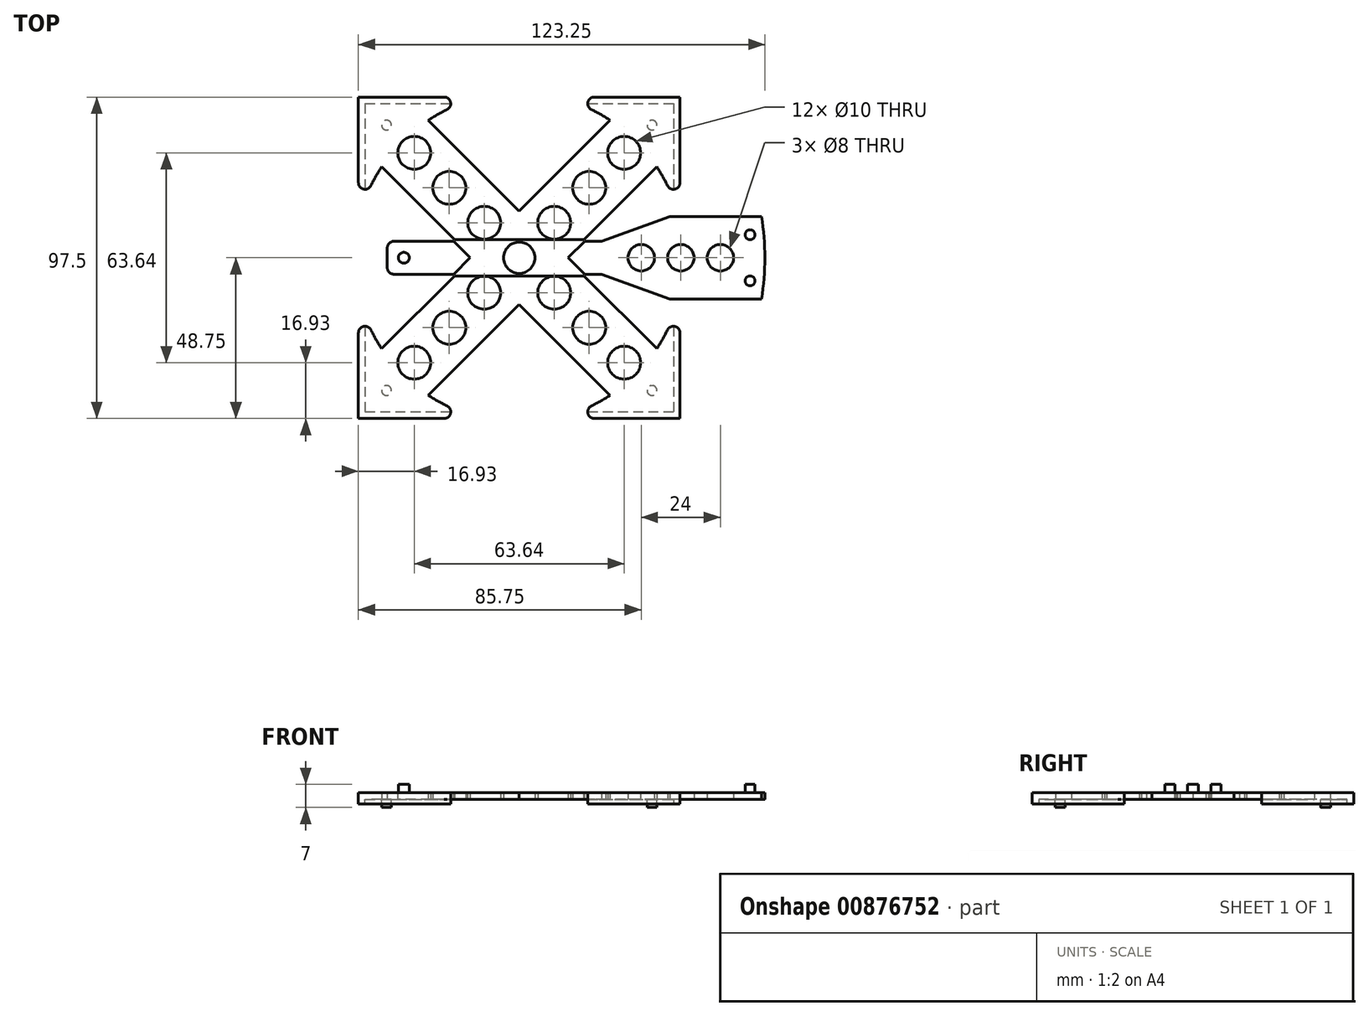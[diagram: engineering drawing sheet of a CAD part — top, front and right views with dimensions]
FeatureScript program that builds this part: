
annotation { "Feature Type Name" : "Feature", "Feature Type Description" : "" }
export const myFeature = defineFeature(function(context is Context, id is Id, definition is map)
    precondition{}
    {
        {
            var Q0;
            Q0=qCreatedBy(makeId("Top.planeOp"),FACE);
            var sketch = newSketch(context, id + "F0", { "sketchPlane" : qUnion([Q0])});
            skLineSegment(sketch, "E0.bottom", {"start": v(-48.75, 48.75) * mm, "end": v(-11.11, 48.75) * mm});
            skLineSegment(sketch, "E0.top", {"start": v(-48.75, -48.75) * mm, "end": v(-11.11, -48.75) * mm});
            skLineSegment(sketch, "E0.left", {"start": v(-48.75, 48.75) * mm, "end": v(-48.75, 11.11) * mm});
            skLineSegment(sketch, "E0.right", {"start": v(48.75, 48.75) * mm, "end": v(48.75, 11.11) * mm});
            skPoint(sketch, "E0.middle", {"position": v(0, 0) * mm});
            skLineSegment(sketch, "E1.trimOffspring", {"start": v(-48.75, -11.11) * mm, "end": v(-48.75, -48.75) * mm});
            skLineSegment(sketch, "E2.trimOffspring", {"start": v(48.75, -11.11) * mm, "end": v(48.75, -48.75) * mm});
            skArc(sketch, "E3", {"start": v(-11.11, 48.75) * mm, "mid": v(-19.66, 45.97) * mm, "end": v(-27.57, 41.71) * mm});
            skLineSegment(sketch, "E4", {"start": v(-41.71, 27.57) * mm, "end": v(-14.14, 0) * mm});
            skLineSegment(sketch, "E5", {"start": v(41.71, -27.57) * mm, "end": v(14.14, 0) * mm});
            skLineSegment(sketch, "E6", {"start": v(27.57, 41.71) * mm, "end": v(0, 14.14) * mm});
            skLineSegment(sketch, "E7", {"start": v(-27.57, -41.71) * mm, "end": v(0, -14.14) * mm});
            skLineSegment(sketch, "E8.trimOffspring", {"start": v(11.11, 48.75) * mm, "end": v(48.75, 48.75) * mm});
            skArc(sketch, "E9.trimOffspring", {"start": v(11.11, -48.75) * mm, "mid": v(19.66, -45.97) * mm, "end": v(27.57, -41.71) * mm});
            skLineSegment(sketch, "E10.trimOffspring", {"start": v(11.11, -48.75) * mm, "end": v(48.75, -48.75) * mm});
            skArc(sketch, "E11.trimOffspring", {"start": v(-48.75, -11.11) * mm, "mid": v(-45.97, -19.66) * mm, "end": v(-41.71, -27.57) * mm});
            skLineSegment(sketch, "E12", {"start": v(0, -14.14) * mm, "end": v(0, 14.14) * mm, "construction": true});
            skLineSegment(sketch, "E13", {"start": v(-14.14, 0) * mm, "end": v(14.14, 0) * mm, "construction": true});
            skArc(sketch, "E14.trimOffspring", {"start": v(27.57, 41.71) * mm, "mid": v(19.66, 45.97) * mm, "end": v(11.11, 48.75) * mm});
            skArc(sketch, "E15.trimOffspring", {"start": v(-41.71, 27.57) * mm, "mid": v(-45.97, 19.66) * mm, "end": v(-48.75, 11.11) * mm});
            skArc(sketch, "E16.trimOffspring", {"start": v(-27.57, -41.71) * mm, "mid": v(-19.66, -45.97) * mm, "end": v(-11.11, -48.75) * mm});
            skLineSegment(sketch, "E17.trimOffspring", {"start": v(0, 14.14) * mm, "end": v(-27.57, 41.71) * mm});
            skLineSegment(sketch, "E18.trimOffspring", {"start": v(-14.14, 0) * mm, "end": v(-41.71, -27.57) * mm});
            skLineSegment(sketch, "E19.trimOffspring", {"start": v(0, -14.14) * mm, "end": v(27.57, -41.71) * mm});
            skLineSegment(sketch, "E20.trimOffspring", {"start": v(14.14, 0) * mm, "end": v(41.71, 27.57) * mm});
            skArc(sketch, "E21", {"start": v(48.75, 11.11) * mm, "mid": v(45.97, 19.66) * mm, "end": v(41.71, 27.57) * mm});
            skArc(sketch, "E22", {"start": v(41.71, -27.57) * mm, "mid": v(45.97, -19.66) * mm, "end": v(48.75, -11.11) * mm});
            skCircle(sketch, "E23", {"center": v(0, 0) * mm, "radius": 5 * mm});
            skCircle(sketch, "E24", {"center": v(-31.82, 31.82) * mm, "radius": 5 * mm});
            skCircle(sketch, "E25", {"center": v(-21.21, 21.21) * mm, "radius": 5 * mm});
            skCircle(sketch, "E26", {"center": v(-10.6, 10.6) * mm, "radius": 5 * mm});
            skCircle(sketch, "E27", {"center": v(10.6, -10.6) * mm, "radius": 5 * mm});
            skCircle(sketch, "E28", {"center": v(21.21, -21.21) * mm, "radius": 5 * mm});
            skCircle(sketch, "E29", {"center": v(31.82, -31.82) * mm, "radius": 5 * mm});
            skCircle(sketch, "E30", {"center": v(-10.6, -10.6) * mm, "radius": 5 * mm});
            skCircle(sketch, "E31", {"center": v(-21.21, -21.21) * mm, "radius": 5 * mm});
            skCircle(sketch, "E32", {"center": v(-31.82, -31.82) * mm, "radius": 5 * mm});
            skCircle(sketch, "E33", {"center": v(31.82, 31.82) * mm, "radius": 5 * mm});
            skCircle(sketch, "E34", {"center": v(21.21, 21.21) * mm, "radius": 5 * mm});
            skCircle(sketch, "E35", {"center": v(10.6, 10.6) * mm, "radius": 5 * mm});
            skLineSegment(sketch, "E36", {"start": v(0, 0) * mm, "end": v(-10.6, 10.6) * mm, "construction": true});
            skLineSegment(sketch, "E37", {"start": v(-10.6, 10.6) * mm, "end": v(-21.21, 21.21) * mm, "construction": true});
            skLineSegment(sketch, "E38", {"start": v(-21.21, 21.21) * mm, "end": v(-31.82, 31.82) * mm, "construction": true});
            skLineSegment(sketch, "E39", {"start": v(0, 0) * mm, "end": v(10.6, -10.6) * mm, "construction": true});
            skLineSegment(sketch, "E40", {"start": v(10.6, -10.6) * mm, "end": v(21.21, -21.21) * mm, "construction": true});
            skLineSegment(sketch, "E41", {"start": v(21.21, -21.21) * mm, "end": v(31.82, -31.82) * mm, "construction": true});
            skLineSegment(sketch, "E42", {"start": v(0, 0) * mm, "end": v(10.6, 10.6) * mm, "construction": true});
            skLineSegment(sketch, "E43", {"start": v(10.6, 10.6) * mm, "end": v(21.21, 21.21) * mm, "construction": true});
            skLineSegment(sketch, "E44", {"start": v(21.21, 21.21) * mm, "end": v(31.82, 31.82) * mm, "construction": true});
            skLineSegment(sketch, "E45", {"start": v(0, 0) * mm, "end": v(-10.6, -10.6) * mm, "construction": true});
            skLineSegment(sketch, "E46", {"start": v(-10.6, -10.6) * mm, "end": v(-21.21, -21.21) * mm, "construction": true});
            skLineSegment(sketch, "E47", {"start": v(-21.21, -21.21) * mm, "end": v(-31.82, -31.82) * mm, "construction": true});
            skLineSegment(sketch, "E48", {"start": v(-48.75, 48.75) * mm, "end": v(48.75, -48.75) * mm, "construction": true});
            skLineSegment(sketch, "E49", {"start": v(-48.75, -48.75) * mm, "end": v(48.75, 48.75) * mm, "construction": true});
            skSolve(sketch);
        }
        {
            var Q0;
            Q0 = qSketchRegion(id + "F0", true);
            extrude(context, id + "F1", {"entities" : qUnion([Q0]), "depth" : 2 * mm, "offsetDistance" : 25 * mm});
        }
        {
            var Q0;
            Q0=makeQuery(id+"F1.opExtrude","CAP_FACE",FACE,{"disambiguationData":[OSD([sQuery(id+"F0.wireOp",EDGE,"E0.bottom"),sQuery(id+"F0.wireOp",EDGE,"E0.top"),sQuery(id+"F0.wireOp",EDGE,"E0.left"),sQuery(id+"F0.wireOp",EDGE,"E0.right"),sQuery(id+"F0.wireOp",EDGE,"uPJQegbE-9fc7-hFGx-GEUX-qmVaFmSYMwRc.bottom"),sQuery(id+"F0.wireOp",EDGE,"uPJQegbE-9fc7-hFGx-GEUX-qmVaFmSYMwRc.top"),sQuery(id+"F0.wireOp",EDGE,"uPJQegbE-9fc7-hFGx-GEUX-qmVaFmSYMwRc.right"),sQuery(id+"F0.wireOp",EDGE,"vvGm7cAz-0FTD-1KYK-Jbby-7V5ZuqElzfrb.bottom"),sQuery(id+"F0.wireOp",EDGE,"vvGm7cAz-0FTD-1KYK-Jbby-7V5ZuqElzfrb.top"),sQuery(id+"F0.wireOp",EDGE,"E1.trimOffspring"),sQuery(id+"F0.wireOp",EDGE,"E2.trimOffspring"),sQuery(id+"F0.wireOp",EDGE,"WdK1YdKJ-L1pb-JJgU-uWy7-1bSEALKaV5mm"),sQuery(id+"F0.wireOp",EDGE,"E3")])],"isStart":true});
            var sketch = newSketch(context, id + "F2", { "sketchPlane" : qUnion([Q0])});
            skLineSegment(sketch, "E50.bottom", {"start": v(17.73, -46.75) * mm, "end": v(46.75, -46.75) * mm});
            skLineSegment(sketch, "E50.top", {"start": v(17.73, 46.75) * mm, "end": v(46.75, 46.75) * mm});
            skLineSegment(sketch, "E50.left", {"start": v(46.75, -46.75) * mm, "end": v(46.75, -17.73) * mm});
            skLineSegment(sketch, "E50.right", {"start": v(-46.75, -46.75) * mm, "end": v(-46.75, -17.73) * mm});
            skLineSegment(sketch, "E51", {"start": v(-46.75, -46.75) * mm, "end": v(46.75, 46.75) * mm, "construction": true});
            skLineSegment(sketch, "E52.bottom", {"start": v(-48.75, 48.75) * mm, "end": v(-11.11, 48.75) * mm});
            skLineSegment(sketch, "E52.top", {"start": v(-48.75, -48.75) * mm, "end": v(-11.11, -48.75) * mm});
            skLineSegment(sketch, "E52.left", {"start": v(-48.75, 48.75) * mm, "end": v(-48.75, 11.11) * mm});
            skLineSegment(sketch, "E52.right", {"start": v(48.75, 48.75) * mm, "end": v(48.75, 11.11) * mm});
            skArc(sketch, "E53", {"start": v(-11.11, 48.75) * mm, "mid": v(-14.46, 47.86) * mm, "end": v(-17.73, 46.75) * mm});
            skLineSegment(sketch, "E54.trimOffspring", {"start": v(11.11, 48.75) * mm, "end": v(48.75, 48.75) * mm});
            skLineSegment(sketch, "E55.trimOffspring", {"start": v(-46.75, 46.75) * mm, "end": v(-17.73, 46.75) * mm});
            skArc(sketch, "E56.trimOffspring", {"start": v(17.73, 46.75) * mm, "mid": v(14.46, 47.86) * mm, "end": v(11.11, 48.75) * mm});
            skLineSegment(sketch, "E57.trimOffspring", {"start": v(46.75, 17.73) * mm, "end": v(46.75, 46.75) * mm});
            skLineSegment(sketch, "E58.trimOffspring", {"start": v(48.75, -11.11) * mm, "end": v(48.75, -48.75) * mm});
            skArc(sketch, "E59.trimOffspring", {"start": v(48.75, 11.11) * mm, "mid": v(47.86, 14.46) * mm, "end": v(46.75, 17.73) * mm});
            skArc(sketch, "E60.trimOffspring", {"start": v(46.75, -17.73) * mm, "mid": v(47.86, -14.46) * mm, "end": v(48.75, -11.11) * mm});
            skLineSegment(sketch, "E61.trimOffspring", {"start": v(-46.75, -46.75) * mm, "end": v(-17.73, -46.75) * mm});
            skLineSegment(sketch, "E62.trimOffspring", {"start": v(11.11, -48.75) * mm, "end": v(48.75, -48.75) * mm});
            skArc(sketch, "E63.trimOffspring", {"start": v(11.11, -48.75) * mm, "mid": v(14.46, -47.86) * mm, "end": v(17.73, -46.75) * mm});
            skArc(sketch, "E64.trimOffspring", {"start": v(-17.73, -46.75) * mm, "mid": v(-14.46, -47.86) * mm, "end": v(-11.11, -48.75) * mm});
            skLineSegment(sketch, "E65.trimOffspring", {"start": v(-46.75, 17.73) * mm, "end": v(-46.75, 46.75) * mm});
            skLineSegment(sketch, "E66.trimOffspring", {"start": v(-48.75, -11.11) * mm, "end": v(-48.75, -48.75) * mm});
            skArc(sketch, "E67.trimOffspring", {"start": v(-48.75, -11.11) * mm, "mid": v(-47.86, -14.46) * mm, "end": v(-46.75, -17.73) * mm});
            skArc(sketch, "E68.trimOffspring", {"start": v(-46.75, 17.73) * mm, "mid": v(-47.86, 14.46) * mm, "end": v(-48.75, 11.11) * mm});
            skSolve(sketch);
        }
        {
            var Q0;
            Q0 = qSketchRegion(id + "F2", true);
            extrude(context, id + "F3", {"entities" : qUnion([Q0]), "operationType" : NewBodyOperationType.ADD, "depth" : 1.5 * mm, "offsetDistance" : 25 * mm});
        }
        {
            var Q0;
            {var subQ0=sQuery(id+"F0.wireOp",EDGE,"E3");Q0=makeQuery(id+"F3.boolean.opBoolean","SPLIT",FACE,{"disambiguationData":[TD([makeQuery(id+"F1.opExtrude","SWEPT_FACE",FACE,{"disambiguationData":[OSD([subQ0])]})])],"derivedFrom":makeQuery(id+"F1.opExtrude","CAP_FACE",FACE,{"disambiguationData":[OSD([sQuery(id+"F0.wireOp",EDGE,"E0.bottom"),sQuery(id+"F0.wireOp",EDGE,"E0.top"),sQuery(id+"F0.wireOp",EDGE,"E0.left"),sQuery(id+"F0.wireOp",EDGE,"E0.right"),sQuery(id+"F0.wireOp",EDGE,"uPJQegbE-9fc7-hFGx-GEUX-qmVaFmSYMwRc.bottom"),sQuery(id+"F0.wireOp",EDGE,"uPJQegbE-9fc7-hFGx-GEUX-qmVaFmSYMwRc.top"),sQuery(id+"F0.wireOp",EDGE,"uPJQegbE-9fc7-hFGx-GEUX-qmVaFmSYMwRc.right"),sQuery(id+"F0.wireOp",EDGE,"vvGm7cAz-0FTD-1KYK-Jbby-7V5ZuqElzfrb.bottom"),sQuery(id+"F0.wireOp",EDGE,"vvGm7cAz-0FTD-1KYK-Jbby-7V5ZuqElzfrb.top"),sQuery(id+"F0.wireOp",EDGE,"E1.trimOffspring"),sQuery(id+"F0.wireOp",EDGE,"E2.trimOffspring"),sQuery(id+"F0.wireOp",EDGE,"WdK1YdKJ-L1pb-JJgU-uWy7-1bSEALKaV5mm"),subQ0])],"isStart":true})});}
            var sketch = newSketch(context, id + "F4", { "sketchPlane" : qUnion([Q0])});
            skLineSegment(sketch, "E69.bottom", {"start": v(-40.25, 40.25) * mm, "end": v(40.25, 40.25) * mm, "construction": true});
            skLineSegment(sketch, "E69.top", {"start": v(-40.25, -40.25) * mm, "end": v(40.25, -40.25) * mm, "construction": true});
            skLineSegment(sketch, "E69.left", {"start": v(-40.25, 40.25) * mm, "end": v(-40.25, -40.25) * mm, "construction": true});
            skLineSegment(sketch, "E69.right", {"start": v(40.25, 40.25) * mm, "end": v(40.25, -40.25) * mm, "construction": true});
            skLineSegment(sketch, "E70", {"start": v(-40.25, 40.25) * mm, "end": v(40.25, -40.25) * mm, "construction": true});
            skLineSegment(sketch, "E71", {"start": v(40.25, 40.25) * mm, "end": v(-40.25, -40.25) * mm, "construction": true});
            skCircle(sketch, "E72", {"center": v(-40.25, 40.25) * mm, "radius": 1.5 * mm});
            skCircle(sketch, "E73", {"center": v(40.25, 40.25) * mm, "radius": 1.5 * mm});
            skCircle(sketch, "E74", {"center": v(40.25, -40.25) * mm, "radius": 1.5 * mm});
            skCircle(sketch, "E75", {"center": v(-40.25, -40.25) * mm, "radius": 1.5 * mm});
            skSolve(sketch);
        }
        {
            var Q0;
            Q0 = qSketchRegion(id + "F4", true);
            extrude(context, id + "F5", {"entities" : qUnion([Q0]), "operationType" : NewBodyOperationType.ADD, "depth" : 2.5 * mm, "offsetDistance" : 25 * mm});
        }
        {
            var Q0;
            Q0=qCreatedBy(makeId("Top.planeOp"),FACE);
            cPlane(context, id + "F6", {"entities" : qUnion([Q0]), "cplaneType" : CPlaneType.OFFSET, "offset" : 1 * mm, "width" : 150 * mm, "height" : 150 * mm});
        }
        {
            var Q0;
            Q0=qCreatedBy(makeId("Top.planeOp"),FACE);
            var sketch = newSketch(context, id + "F7", { "sketchPlane" : qUnion([Q0])});
            skLineSegment(sketch, "E76.bottom", {"start": v(-40, 5) * mm, "end": v(25, 5) * mm});
            skLineSegment(sketch, "E76.top", {"start": v(-40, -5) * mm, "end": v(25, -5) * mm});
            skLineSegment(sketch, "E76.left", {"start": v(-40, 5) * mm, "end": v(-40, -5) * mm});
            skLineSegment(sketch, "E76.right", {"start": v(25, 5) * mm, "end": v(25, -5) * mm});
            skLineSegment(sketch, "E77.bottom", {"start": v(73.44, 12.5) * mm, "end": v(45.6, 12.5) * mm});
            skLineSegment(sketch, "E77.top", {"start": v(73.44, -12.5) * mm, "end": v(45.6, -12.5) * mm});
            skLineSegment(sketch, "E77.right", {"start": v(45.6, 12.5) * mm, "end": v(45.6, -12.5) * mm, "construction": true});
            skLineSegment(sketch, "E78", {"start": v(25, -5) * mm, "end": v(45.6, -12.5) * mm});
            skLineSegment(sketch, "E79", {"start": v(25, 5) * mm, "end": v(45.6, 12.5) * mm});
            skLineSegment(sketch, "E80", {"start": v(-40, 0) * mm, "end": v(73.44, 0) * mm, "construction": true});
            skArc(sketch, "E81", {"start": v(73.44, -12.5) * mm, "mid": v(74.5, 0) * mm, "end": v(73.44, 12.5) * mm});
            skCircle(sketch, "E82", {"center": v(37, 0) * mm, "radius": 4 * mm});
            skCircle(sketch, "E83", {"center": v(49, 0) * mm, "radius": 4 * mm});
            skCircle(sketch, "E84", {"center": v(61, 0) * mm, "radius": 4 * mm});
            skLineSegment(sketch, "E85", {"start": v(37, 0) * mm, "end": v(49, 0) * mm, "construction": true});
            skLineSegment(sketch, "E86", {"start": v(49, 0) * mm, "end": v(61, 0) * mm, "construction": true});
            skSolve(sketch);
        }
        {
            var Q0;
            Q0 = qSketchRegion(id + "F7", true);
            extrude(context, id + "F8", {"entities" : qUnion([Q0]), "depth" : 2 * mm, "offsetDistance" : 25 * mm});
        }
        {
            var Q0;
            Q0=makeQuery(id+"F8.opExtrude","CAP_FACE",FACE,{"disambiguationData":[OSD([sQuery(id+"F7.wireOp",EDGE,"E76.bottom"),sQuery(id+"F7.wireOp",EDGE,"E76.top"),sQuery(id+"F7.wireOp",EDGE,"E76.left"),sQuery(id+"F7.wireOp",EDGE,"E77.bottom"),sQuery(id+"F7.wireOp",EDGE,"E77.top"),sQuery(id+"F7.wireOp",EDGE,"E78"),sQuery(id+"F7.wireOp",EDGE,"E79"),sQuery(id+"F7.wireOp",EDGE,"E81")])],"isStart":false});
            var sketch = newSketch(context, id + "F9", { "sketchPlane" : qUnion([Q0])});
            skCircle(sketch, "E87", {"center": v(-35, 0) * mm, "radius": 1.65 * mm});
            skCircle(sketch, "E88", {"center": v(70, 7) * mm, "radius": 1.5 * mm});
            skCircle(sketch, "E89", {"center": v(70, -7) * mm, "radius": 1.5 * mm});
            skLineSegment(sketch, "E90", {"start": v(70, 7) * mm, "end": v(70, -7) * mm, "construction": true});
            skLineSegment(sketch, "E91", {"start": v(-35, 0) * mm, "end": v(70, 0) * mm, "construction": true});
            skSolve(sketch);
        }
        {
            var Q0;
            Q0 = qSketchRegion(id + "F9", true);
            extrude(context, id + "F10", {"entities" : qUnion([Q0]), "operationType" : NewBodyOperationType.ADD, "depth" : 2.5 * mm, "offsetDistance" : 25 * mm});
        }
        {
            var Q0;
            Q0=qCreatedBy(id+"F6.planeOp",FACE);
            var sketch = newSketch(context, id + "F11", { "sketchPlane" : qUnion([Q0])});
            skLineSegment(sketch, "E92", {"start": v(-19.14, 5) * mm, "end": v(-14.14, 0) * mm, "construction": true});
            skLineSegment(sketch, "E93", {"start": v(-14.14, 0) * mm, "end": v(-19.14, -5) * mm, "construction": true});
            skLineSegment(sketch, "E94", {"start": v(-19.14, -5) * mm, "end": v(19.14, -5) * mm, "construction": true});
            skLineSegment(sketch, "E95", {"start": v(19.14, -5) * mm, "end": v(14.14, 0) * mm, "construction": true});
            skLineSegment(sketch, "E96", {"start": v(14.14, 0) * mm, "end": v(19.14, 5) * mm, "construction": true});
            skLineSegment(sketch, "E97", {"start": v(19.14, 5) * mm, "end": v(-19.14, 5) * mm, "construction": true});
            skLineSegment(sketch, "E98.0", {"start": v(14.85, 0) * mm, "end": v(20.35, 5.5) * mm});
            skLineSegment(sketch, "E98.1", {"start": v(-20.35, 5.5) * mm, "end": v(-14.85, 0) * mm});
            skLineSegment(sketch, "E98.2", {"start": v(-14.85, 0) * mm, "end": v(-20.35, -5.5) * mm});
            skLineSegment(sketch, "E98.3", {"start": v(20.35, 5.5) * mm, "end": v(-20.35, 5.5) * mm});
            skLineSegment(sketch, "E98.4", {"start": v(-20.35, -5.5) * mm, "end": v(20.35, -5.5) * mm});
            skLineSegment(sketch, "E98.5", {"start": v(20.35, -5.5) * mm, "end": v(14.85, 0) * mm});
            skCircle(sketch, "E99", {"center": v(0, 0) * mm, "radius": 4.75 * mm});
            skSolve(sketch);
        }
        {
            var Q0;
            Q0 = qSketchRegion(id + "F11", true);
            extrude(context, id + "F12", {"entities" : qUnion([Q0]), "operationType" : NewBodyOperationType.REMOVE, "depth" : 1 * mm, "offsetDistance" : 25 * mm});
        }
        {
            var Q0;
            Q0 = qSketchRegion(id + "F11", true);
            extrude(context, id + "F13", {"entities" : qUnion([Q0]), "operationType" : NewBodyOperationType.REMOVE, "oppositeDirection" : true, "depth" : 1 * mm, "offsetDistance" : 25 * mm});
        }
        {
            var Q0;
            Q0=makeQuery(id+"F3.boolean.opBoolean","MERGE",EDGE,{"derivedFrom":[makeQuery(id+"F1.opExtrude","SWEPT_EDGE",EDGE,{"disambiguationData":[OSD([sQuery(id+"F0.wireOp",EDGE,"E0.left"),sQuery(id+"F0.wireOp",EDGE,"E15.trimOffspring")])]}),makeQuery(id+"F3.opExtrude","SWEPT_EDGE",EDGE,{"disambiguationData":[OSD([sQuery(id+"F2.wireOp",EDGE,"E66.trimOffspring"),sQuery(id+"F2.wireOp",EDGE,"E67.trimOffspring")])]})]});
            var Q1;
            Q1=makeQuery(id+"F3.boolean.opBoolean","MERGE",EDGE,{"derivedFrom":[makeQuery(id+"F1.opExtrude","SWEPT_EDGE",EDGE,{"disambiguationData":[OSD([sQuery(id+"F0.wireOp",EDGE,"E0.bottom"),sQuery(id+"F0.wireOp",EDGE,"E3")])]}),makeQuery(id+"F3.opExtrude","SWEPT_EDGE",EDGE,{"disambiguationData":[OSD([sQuery(id+"F2.wireOp",EDGE,"E52.top"),sQuery(id+"F2.wireOp",EDGE,"E64.trimOffspring")])]})]});
            var Q2;
            Q2=makeQuery(id+"F3.boolean.opBoolean","MERGE",EDGE,{"derivedFrom":[makeQuery(id+"F1.opExtrude","SWEPT_EDGE",EDGE,{"disambiguationData":[OSD([sQuery(id+"F0.wireOp",EDGE,"E8.trimOffspring"),sQuery(id+"F0.wireOp",EDGE,"E14.trimOffspring")])]}),makeQuery(id+"F3.opExtrude","SWEPT_EDGE",EDGE,{"disambiguationData":[OSD([sQuery(id+"F2.wireOp",EDGE,"E62.trimOffspring"),sQuery(id+"F2.wireOp",EDGE,"E63.trimOffspring")])]})]});
            var Q3;
            Q3=makeQuery(id+"F3.boolean.opBoolean","MERGE",EDGE,{"derivedFrom":[makeQuery(id+"F1.opExtrude","SWEPT_EDGE",EDGE,{"disambiguationData":[OSD([sQuery(id+"F0.wireOp",EDGE,"E0.right"),sQuery(id+"F0.wireOp",EDGE,"E21")])]}),makeQuery(id+"F3.opExtrude","SWEPT_EDGE",EDGE,{"disambiguationData":[OSD([sQuery(id+"F2.wireOp",EDGE,"E58.trimOffspring"),sQuery(id+"F2.wireOp",EDGE,"E60.trimOffspring")])]})]});
            var Q4;
            Q4=makeQuery(id+"F3.boolean.opBoolean","MERGE",EDGE,{"derivedFrom":[makeQuery(id+"F1.opExtrude","SWEPT_EDGE",EDGE,{"disambiguationData":[OSD([sQuery(id+"F0.wireOp",EDGE,"E2.trimOffspring"),sQuery(id+"F0.wireOp",EDGE,"E22")])]}),makeQuery(id+"F3.opExtrude","SWEPT_EDGE",EDGE,{"disambiguationData":[OSD([sQuery(id+"F2.wireOp",EDGE,"E52.right"),sQuery(id+"F2.wireOp",EDGE,"E59.trimOffspring")])]})]});
            var Q5;
            Q5=makeQuery(id+"F3.boolean.opBoolean","MERGE",EDGE,{"derivedFrom":[makeQuery(id+"F1.opExtrude","SWEPT_EDGE",EDGE,{"disambiguationData":[OSD([sQuery(id+"F0.wireOp",EDGE,"E1.trimOffspring"),sQuery(id+"F0.wireOp",EDGE,"E11.trimOffspring")])]}),makeQuery(id+"F3.opExtrude","SWEPT_EDGE",EDGE,{"disambiguationData":[OSD([sQuery(id+"F2.wireOp",EDGE,"E52.left"),sQuery(id+"F2.wireOp",EDGE,"E68.trimOffspring")])]})]});
            var Q6;
            Q6=makeQuery(id+"F3.boolean.opBoolean","MERGE",EDGE,{"derivedFrom":[makeQuery(id+"F1.opExtrude","SWEPT_EDGE",EDGE,{"disambiguationData":[OSD([sQuery(id+"F0.wireOp",EDGE,"E0.top"),sQuery(id+"F0.wireOp",EDGE,"E16.trimOffspring")])]}),makeQuery(id+"F3.opExtrude","SWEPT_EDGE",EDGE,{"disambiguationData":[OSD([sQuery(id+"F2.wireOp",EDGE,"E52.bottom"),sQuery(id+"F2.wireOp",EDGE,"E53")])]})]});
            var Q7;
            Q7=makeQuery(id+"F3.boolean.opBoolean","MERGE",EDGE,{"derivedFrom":[makeQuery(id+"F1.opExtrude","SWEPT_EDGE",EDGE,{"disambiguationData":[OSD([sQuery(id+"F0.wireOp",EDGE,"E9.trimOffspring"),sQuery(id+"F0.wireOp",EDGE,"E10.trimOffspring")])]}),makeQuery(id+"F3.opExtrude","SWEPT_EDGE",EDGE,{"disambiguationData":[OSD([sQuery(id+"F2.wireOp",EDGE,"E54.trimOffspring"),sQuery(id+"F2.wireOp",EDGE,"E56.trimOffspring")])]})]});
            var Q8;
            Q8=makeQuery(id+"F8.opExtrude","SWEPT_EDGE",EDGE,{"disambiguationData":[OSD([sQuery(id+"F7.wireOp",EDGE,"E76.bottom"),sQuery(id+"F7.wireOp",EDGE,"E76.left")])]});
            var Q9;
            Q9=makeQuery(id+"F8.opExtrude","SWEPT_EDGE",EDGE,{"disambiguationData":[OSD([sQuery(id+"F7.wireOp",EDGE,"E76.top"),sQuery(id+"F7.wireOp",EDGE,"E76.left")])]});
            fillet(context, id + "F14", {"entities" : qUnion([Q0, Q1, Q2, Q3, Q4, Q5, Q6, Q7, Q8, Q9]), "radius" : 2 * mm, "tangentPropagation" : true, "allowEdgeOverflow" : false});
        }
    });
